# Revit family: Commercial_Shower_System-American_Standard-Glenmere-TU617508_Series
name_source: partatom
category: Plumbing Fixtures
units: mm (PartAtom-declared; Revit-internal decimal feet)

## family parameters
Cut with Voids When Loaded = No
Host = Face
OmniClass Number = 23.45.05.14.17
OmniClass Title = Showers
Part Type = Normal
Room Calculation Point = No
Round Connector Dimension = Use Diameter
Shared = Yes

## types (4) — shared parameters
ADA Compliant = Yes
Assembly Code = D2010710
CW Connection = Yes
CWFU = 3
Cold Water Connection Diameter = 1/2"
Default Elevation = 0"
Description = Glenmere™ 1.8 gpm/6.8 L/min Tub and Shower Trim Kit With Water-Saving Showerhead, Double Ceramic Pressure Balance Cartridge With Lever Handle
Flow Rate = 1.8 gpm(6.8 Lpm)
HW Connection = Yes
HWFU = 3
Hot Water Connection Diameter = 1/2"
IAPMO Compliance = ASSE 1016 / ASME A112.18.1016 / CSA B125.16, ASME A112.18.1 / CSA B125.1, Rated to meet ASSE 1016 @ 1.3gpm
Installation Type = Wall Mounted
Lever Diameter = 7 11/16"
Lever Handle Height = 36"
Manufacturer = American Standard
Product Documentation Link = https://americanstandard.box.com
Product Page URL = https://www.americanstandard-us.com
Showerhead Connection Diameter = 1/2"
Showerhead Diameter = 6 13/16"
Showerhead Height = 77 1/16"
Showerhead Height Constraint = 77 1/16"
Tempered Water Connection = Yes
Tub Connection Diameter = 1/2"
Tub Faucet Height = 18"
Tub Faucet Width = 6 1/16"
URL = https://www.americanstandard-us.com
Vent Connection = No
WFU = 4
Warranty Information = Limited lifetime warranty
Waste Connection = No

## per-type parameters (varying)
| type | Finish | Material |
| TU617508.002 | Metal-American Standard-002-Polished Chrome | Metal-American Standard-002-Polished Chrome |
| TU617508.295 | Metal-American Standard-295-Brushed Nickel | Metal-American Standard-295-Brushed Nickel |
| TU617508.243 | Metal-American Standard-243-Matte Black | Metal-American Standard-243-Matte Black |
| TU617508.278 | Metal-American Standard-278-Legacy Bronze | Metal-American Standard-278-Legacy Bronze |

note: column(s) folded — value = type name in every type: Model

## geometry (parser evidence)
native form markers: Sweep x13
no freeform markers — native parametric forms only
